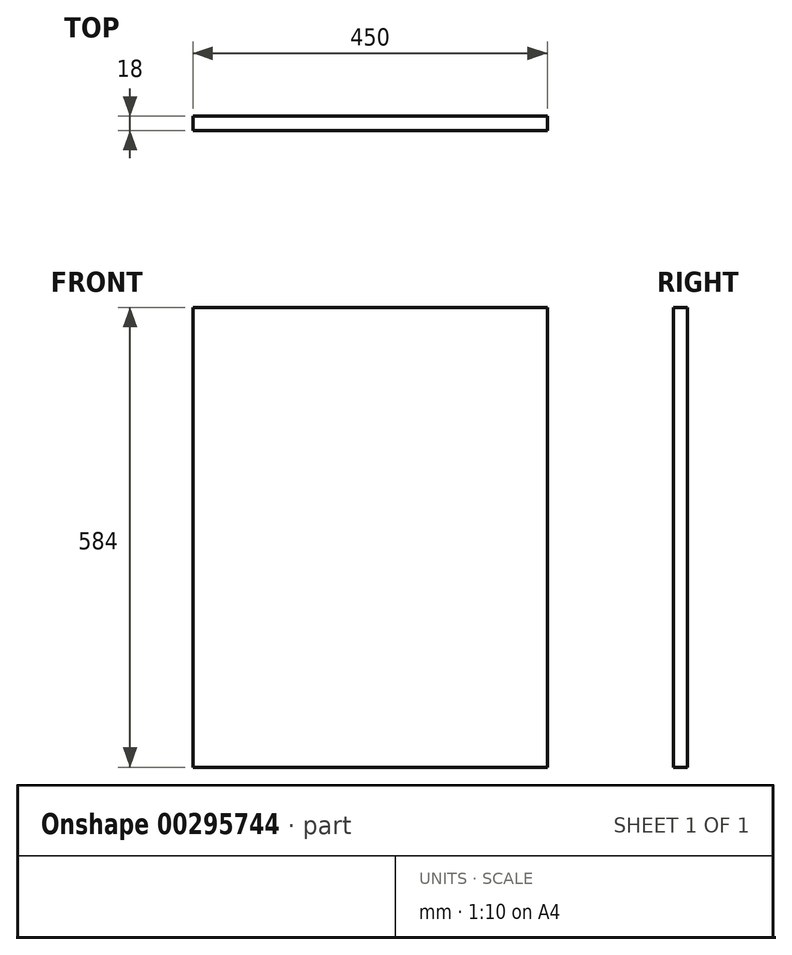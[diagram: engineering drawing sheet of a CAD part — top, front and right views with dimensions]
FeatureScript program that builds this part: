
annotation { "Feature Type Name" : "Feature", "Feature Type Description" : "" }
export const myFeature = defineFeature(function(context is Context, id is Id, definition is map)
    precondition{}
    {
        {
            var Q0;
            Q0=qCreatedBy(makeId("Front.planeOp"),FACE);
            var sketch = newSketch(context, id + "F0", { "sketchPlane" : qUnion([Q0])});
            skLineSegment(sketch, "E0.bottom", {"start": v(-212.71, 307.08) * mm, "end": v(237.29, 307.08) * mm});
            skLineSegment(sketch, "E0.top", {"start": v(-212.71, -276.92) * mm, "end": v(237.29, -276.92) * mm});
            skLineSegment(sketch, "E0.left", {"start": v(-212.71, 307.08) * mm, "end": v(-212.71, -276.92) * mm});
            skLineSegment(sketch, "E0.right", {"start": v(237.29, 307.08) * mm, "end": v(237.29, -276.92) * mm});
            skSolve(sketch);
        }
        {
            var Q0;
            Q0 = qSketchRegion(id + "F0", true);
            extrude(context, id + "F1", {"entities" : qUnion([Q0]), "depth" : 18 * mm});
        }
    });
